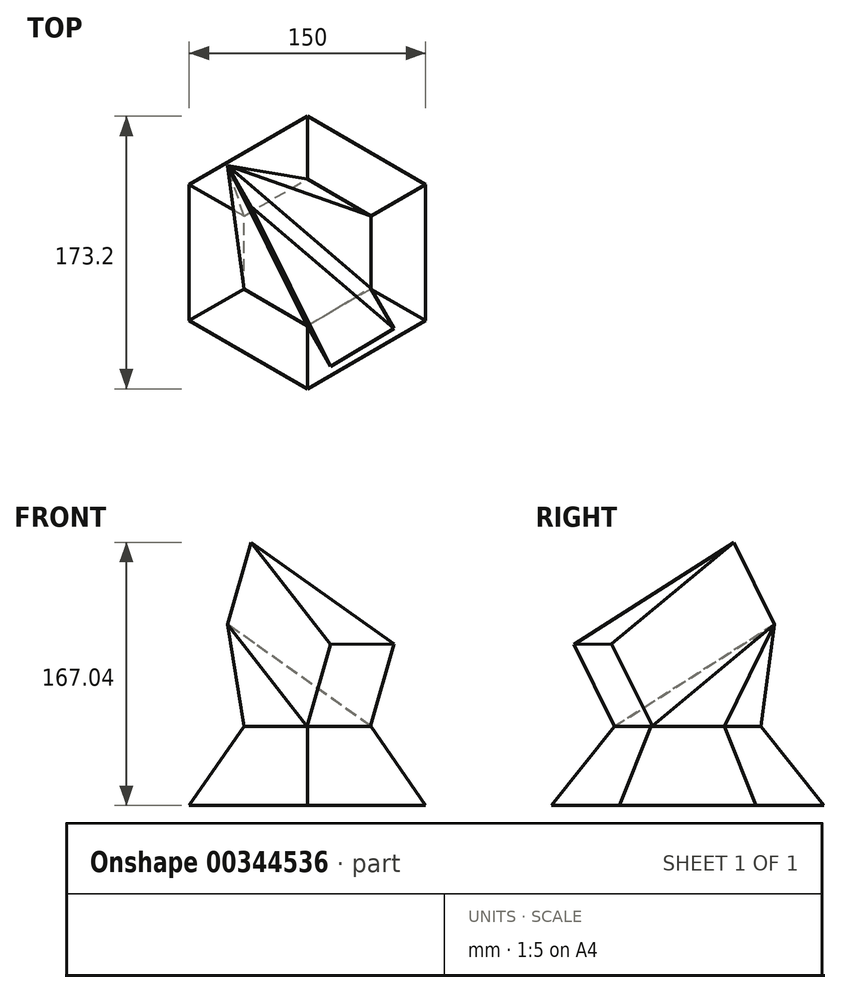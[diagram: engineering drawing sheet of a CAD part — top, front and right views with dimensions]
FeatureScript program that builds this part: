
annotation { "Feature Type Name" : "Feature", "Feature Type Description" : "" }
export const myFeature = defineFeature(function(context is Context, id is Id, definition is map)
    precondition{}
    {
        {
            var Q0;
            Q0=qCreatedBy(makeId("Top.planeOp"),FACE);
            var sketch = newSketch(context, id + "F0", { "sketchPlane" : qUnion([Q0])});
            skCircle(sketch, "E0.cCircle", {"center": v(0, 0) * mm, "radius": 86.6 * mm, "construction": true});
            skLineSegment(sketch, "E0.0", {"start": v(0, 86.6) * mm, "end": v(75, 43.3) * mm});
            skLineSegment(sketch, "E0.1", {"start": v(75, 43.3) * mm, "end": v(75, -43.3) * mm});
            skLineSegment(sketch, "E0.2", {"start": v(75, -43.3) * mm, "end": v(0, -86.6) * mm});
            skLineSegment(sketch, "E0.3", {"start": v(0, -86.6) * mm, "end": v(-75, -43.3) * mm});
            skLineSegment(sketch, "E0.4", {"start": v(-75, -43.3) * mm, "end": v(-75, 43.3) * mm});
            skLineSegment(sketch, "E0.5", {"start": v(-75, 43.3) * mm, "end": v(0, 86.6) * mm});
            skSolve(sketch);
        }
        {
            var Q0;
            Q0=qCreatedBy(makeId("Top.planeOp"),FACE);
            cPlane(context, id + "F1", {"entities" : qUnion([Q0]), "cplaneType" : CPlaneType.OFFSET, "offset" : 50 * mm, "width" : 150 * mm, "height" : 150 * mm});
        }
        {
            var Q0;
            Q0=qCreatedBy(id+"F1.planeOp",FACE);
            var sketch = newSketch(context, id + "F2", { "sketchPlane" : qUnion([Q0])});
            skCircle(sketch, "E1.cCircle", {"center": v(0, 0) * mm, "radius": 46.57 * mm, "construction": true});
            skLineSegment(sketch, "E1.0", {"start": v(0, 46.57) * mm, "end": v(40.33, 23.28) * mm});
            skLineSegment(sketch, "E1.1", {"start": v(40.33, 23.28) * mm, "end": v(40.33, -23.28) * mm});
            skLineSegment(sketch, "E1.2", {"start": v(40.33, -23.28) * mm, "end": v(0, -46.57) * mm});
            skLineSegment(sketch, "E1.3", {"start": v(0, -46.57) * mm, "end": v(-40.33, -23.28) * mm});
            skLineSegment(sketch, "E1.4", {"start": v(-40.33, -23.28) * mm, "end": v(-40.33, 23.28) * mm});
            skLineSegment(sketch, "E1.5", {"start": v(-40.33, 23.28) * mm, "end": v(0, 46.57) * mm});
            skSolve(sketch);
        }
        {
            var Q0;
            Q0=makeQuery(id+"F0.imprint","IMPRINT",FACE,{"disambiguationData":[TD([[makeQuery(id+"F0.imprint","IMPRINT",EDGE,{"derivedFrom":sQuery(id+"F0.wireOp",EDGE,"E0.0")}),-1.0]])]});
            var Q1;
            Q1=makeQuery(id+"F2.imprint","IMPRINT",FACE,{"disambiguationData":[TD([[makeQuery(id+"F2.imprint","IMPRINT",EDGE,{"derivedFrom":sQuery(id+"F2.wireOp",EDGE,"E1.0")}),-1.0]])]});
            loft(context, id + "F3", {"sheetProfilesArray" : [{ "sheetProfileEntities" : qUnion([Q0]) }, { "sheetProfileEntities" : qUnion([Q1]) }]});
        }
        {
            var Q0;
            Q0=qCreatedBy(id+"F1.planeOp",FACE);
            cPlane(context, id + "F4", {"entities" : qUnion([Q0]), "cplaneType" : CPlaneType.OFFSET, "offset" : 65 * mm, "width" : 150 * mm, "height" : 150 * mm});
        }
        {
            var Q0;
            Q0=qCreatedBy(id+"F4.planeOp",FACE);
            var sketch = newSketch(context, id + "F5", { "sketchPlane" : qUnion([Q0])});
            skCircle(sketch, "E2.cCircle", {"center": v(-50.65, 55.15) * mm, "radius": 1.63 * mm, "construction": true});
            skLineSegment(sketch, "E2.0", {"start": v(-49.4, 54.1) * mm, "end": v(-50.92, 53.53) * mm});
            skLineSegment(sketch, "E2.1", {"start": v(-50.92, 53.53) * mm, "end": v(-52.18, 54.58) * mm});
            skLineSegment(sketch, "E2.2", {"start": v(-52.18, 54.58) * mm, "end": v(-51.9, 56.2) * mm});
            skLineSegment(sketch, "E2.3", {"start": v(-51.9, 56.2) * mm, "end": v(-50.37, 56.76) * mm});
            skLineSegment(sketch, "E2.4", {"start": v(-50.37, 56.76) * mm, "end": v(-49.11, 55.7) * mm});
            skLineSegment(sketch, "E2.5", {"start": v(-49.11, 55.7) * mm, "end": v(-49.4, 54.1) * mm});
            skSolve(sketch);
        }
        {
            var Q1;
            Q1=makeQuery(id+"F3.opLoft","CAP_FACE",FACE,{"disambiguationData":[OSD([makeQuery(id+"F2.imprint","IMPRINT",FACE,{"disambiguationData":[TD([[makeQuery(id+"F2.imprint","IMPRINT",EDGE,{"derivedFrom":sQuery(id+"F2.wireOp",EDGE,"E1.0")}),-1.0]])]})])],"isStart":true});
            var Q2;
            Q2=sQuery(id+"F5.wireOp",VERTEX,"E2.cCircle.center");
            loft(context, id + "F6", {"operationType" : NewBodyOperationType.ADD, "sheetProfilesArray" : [{ "sheetProfileEntities" : qUnion([Q1]) }, { "sheetProfileEntities" : qUnion([Q2]) }]});
        }
        {
            var Q0;
            Q0=makeQuery(id+"F6.opLoft","SWEPT_FACE",FACE,{"disambiguationData":[OSD([sQuery(id+"F2.wireOp",EDGE,"E1.1"),sQuery(id+"F2.wireOp",EDGE,"E1.2"),sQuery(id+"F2.wireOp",EDGE,"E1.3")])]});
            cPlane(context, id + "F7", {"entities" : qUnion([Q0]), "cplaneType" : CPlaneType.OFFSET, "offset" : 0 * mm, "width" : 150 * mm, "height" : 150 * mm});
        }
        {
            var Q0;
            Q0=qCreatedBy(id+"F7.planeOp",FACE);
            var sketch = newSketch(context, id + "F8", { "sketchPlane" : qUnion([Q0])});
            skLineSegment(sketch, "E3", {"start": v(-68.65, 100.45) * mm, "end": v(-16.38, -19.31) * mm});
            skLineSegment(sketch, "E4", {"start": v(-16.38, -19.31) * mm, "end": v(25.16, 2.28) * mm});
            skLineSegment(sketch, "E5", {"start": v(25.16, 2.28) * mm, "end": v(-68.65, 100.45) * mm});
            skSolve(sketch);
        }
        {
            var Q0;
            Q0=makeQuery(id+"F8.imprint","IMPRINT",FACE,{"disambiguationData":[TD([[makeQuery(id+"F8.imprint","IMPRINT",EDGE,{"derivedFrom":sQuery(id+"F8.wireOp",EDGE,"E3")}),1.0]])]});
            extrude(context, id + "F9", {"entities" : qUnion([Q0]), "operationType" : NewBodyOperationType.ADD, "depth" : 60 * mm});
        }
        {
            var Q0;
            Q0=makeQuery(id+"F6.opLoft","SWEPT_FACE",FACE,{"disambiguationData":[OSD([sQuery(id+"F2.wireOp",EDGE,"E1.0"),sQuery(id+"F2.wireOp",EDGE,"E1.1"),sQuery(id+"F2.wireOp",EDGE,"E1.2")])]});
            var sketch = newSketch(context, id + "F10", { "sketchPlane" : qUnion([Q0])});
            skSolve(sketch);
        }
        {
            var Q0;
            {var subQ1=sQuery(id+"F2.wireOp",EDGE,"E1.1");var subQ2=sQuery(id+"F2.wireOp",EDGE,"E1.0");var subQ11=sQuery(id+"F5.wireOp",VERTEX,"E2.cCircle.center");Q0=makeQuery(id+"F10.imprint","IMPRINT",FACE,{"disambiguationData":[TD([[makeQuery(id+"F10.imprint","IMPRINT",EDGE,{"derivedFrom":makeQuery(id+"F6.opLoft","SWEPT_EDGE",EDGE,{"disambiguationData":[OSD([subQ2,subQ1,subQ11])]})}),1.0]])]});}
            cPlane(context, id + "F11", {"entities" : qUnion([Q0]), "cplaneType" : CPlaneType.OFFSET, "offset" : 0 * mm, "width" : 150 * mm, "height" : 150 * mm});
        }
    });
